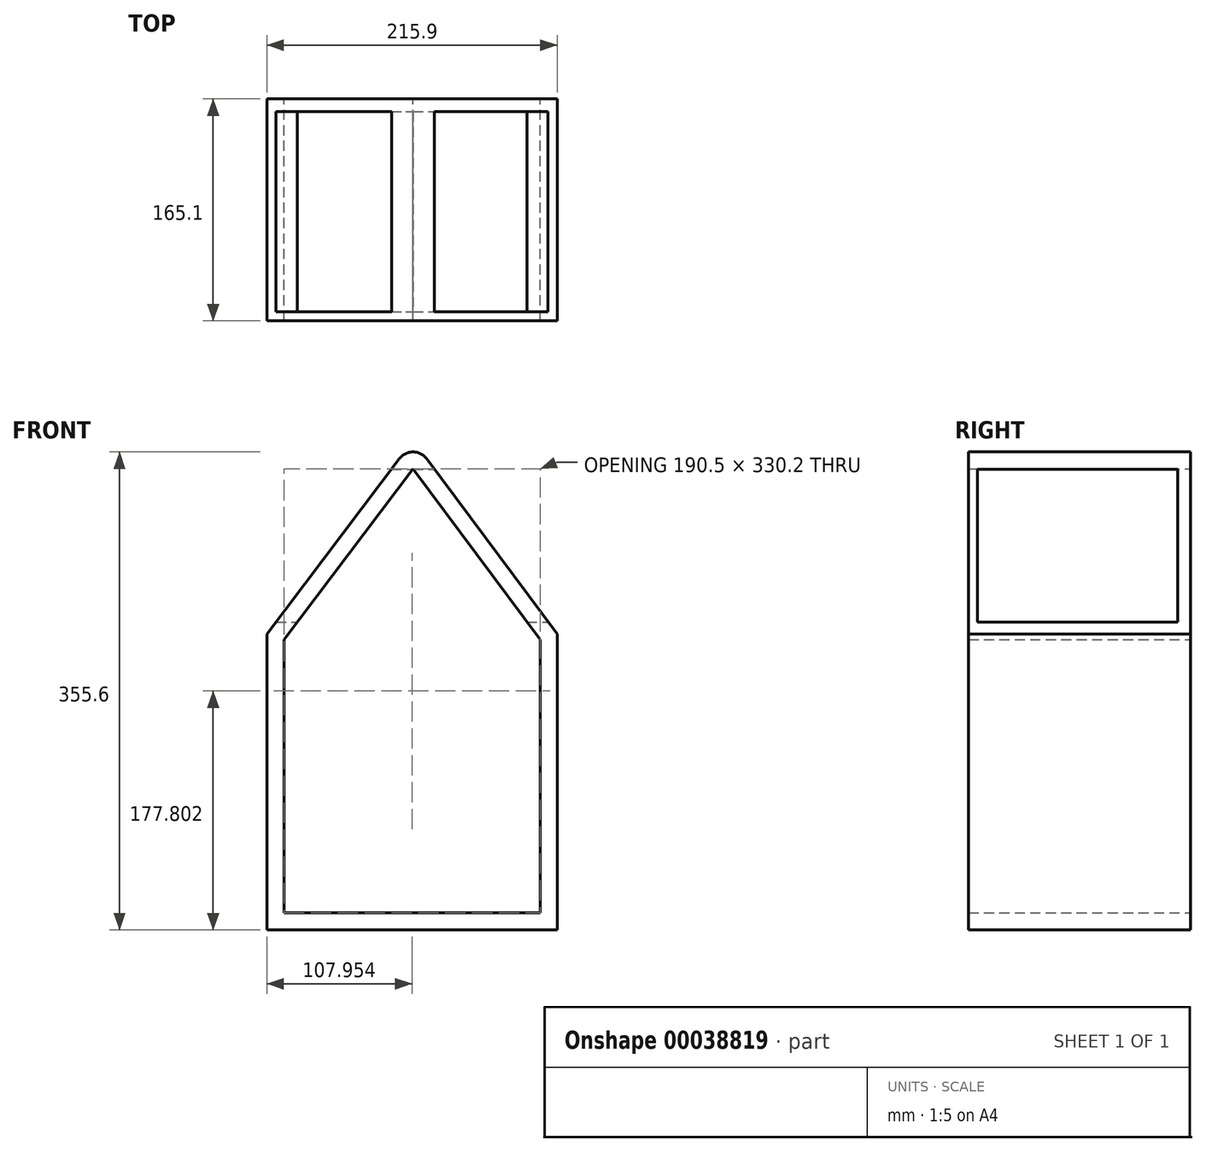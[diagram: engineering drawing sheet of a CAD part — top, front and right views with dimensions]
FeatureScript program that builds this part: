
annotation { "Feature Type Name" : "Feature", "Feature Type Description" : "" }
export const myFeature = defineFeature(function(context is Context, id is Id, definition is map)
    precondition{}
    {
        {
            var Q0;
            Q0=qCreatedBy(makeId("Front.planeOp"),FACE);
            var sketch = newSketch(context, id + "F0", { "sketchPlane" : qUnion([Q0])});
            skLineSegment(sketch, "E0.bottom", {"start": v(-95.96, -139.5) * mm, "end": v(94.54, -139.5) * mm});
            skLineSegment(sketch, "E0.top", {"start": v(-95.96, 63.7) * mm, "end": v(94.54, 63.7) * mm});
            skLineSegment(sketch, "E0.left", {"start": v(-95.96, -139.5) * mm, "end": v(-95.96, 63.7) * mm});
            skLineSegment(sketch, "E0.right", {"start": v(94.54, -139.5) * mm, "end": v(94.54, 63.7) * mm});
            skLineSegment(sketch, "E1", {"start": v(-95.96, 63.7) * mm, "end": v(0, 190.7) * mm});
            skLineSegment(sketch, "E2", {"start": v(0, 190.7) * mm, "end": v(94.54, 63.7) * mm});
            skLineSegment(sketch, "E3.0", {"start": v(0.08, 211.87) * mm, "end": v(107.24, 67.9) * mm});
            skLineSegment(sketch, "E3.1", {"start": v(-108.66, 67.96) * mm, "end": v(0.08, 211.87) * mm});
            skLineSegment(sketch, "E3.2", {"start": v(107.24, -152.2) * mm, "end": v(107.24, 67.9) * mm});
            skLineSegment(sketch, "E3.3", {"start": v(-108.66, -152.2) * mm, "end": v(107.24, -152.2) * mm});
            skLineSegment(sketch, "E3.4", {"start": v(-108.66, -152.2) * mm, "end": v(-108.66, 67.96) * mm});
            skSolve(sketch);
        }
        {
            var Q0;
            Q0=makeQuery(id+"F0.imprint","IMPRINT",FACE,{"disambiguationData":[TD([[makeQuery(id+"F0.imprint","IMPRINT",EDGE,{"derivedFrom":sQuery(id+"F0.wireOp",EDGE,"E0.bottom")}),-1.0]])]});
            extrude(context, id + "F1", {"entities" : qUnion([Q0]), "depth" : 165.1 * mm});
        }
        {
            var Q0;
            Q0=makeQuery(id+"F1.opExtrude","SWEPT_EDGE",EDGE,{"disambiguationData":[OSD([sQuery(id+"F0.wireOp",EDGE,"E3.0"),sQuery(id+"F0.wireOp",EDGE,"E3.1")])]});
            fillet(context, id + "F2", {"entities" : qUnion([Q0]), "radius" : 12.7 * mm, "tangentPropagation" : true, "allowEdgeOverflow" : false});
        }
        {
            var Q0;
            Q0=qCreatedBy(makeId("Right.planeOp"),FACE);
            var sketch = newSketch(context, id + "F3", { "sketchPlane" : qUnion([Q0])});
            skLineSegment(sketch, "E4.bottom", {"start": v(-158.24, 190.66) * mm, "end": v(-9.45, 190.66) * mm});
            skLineSegment(sketch, "E4.top", {"start": v(-158.24, 76.98) * mm, "end": v(-9.45, 76.98) * mm});
            skLineSegment(sketch, "E4.left", {"start": v(-158.24, 190.66) * mm, "end": v(-158.24, 76.98) * mm});
            skLineSegment(sketch, "E4.right", {"start": v(-9.45, 190.66) * mm, "end": v(-9.45, 76.98) * mm});
            skSolve(sketch);
        }
        {
            var Q0;
            Q0=makeQuery(id+"F3.imprint","IMPRINT",FACE,{"disambiguationData":[TD([[makeQuery(id+"F3.imprint","IMPRINT",EDGE,{"derivedFrom":sQuery(id+"F3.wireOp",EDGE,"E4.bottom")}),-1.0]])]});
            extrude(context, id + "F4", {"entities" : qUnion([Q0]), "operationType" : NewBodyOperationType.REMOVE, "oppositeDirection" : true, "depth" : 168.44 * mm, "hasSecondDirection" : true, "secondDirectionOppositeDirection" : false, "secondDirectionDepth" : 150.7 * mm});
        }
    });
